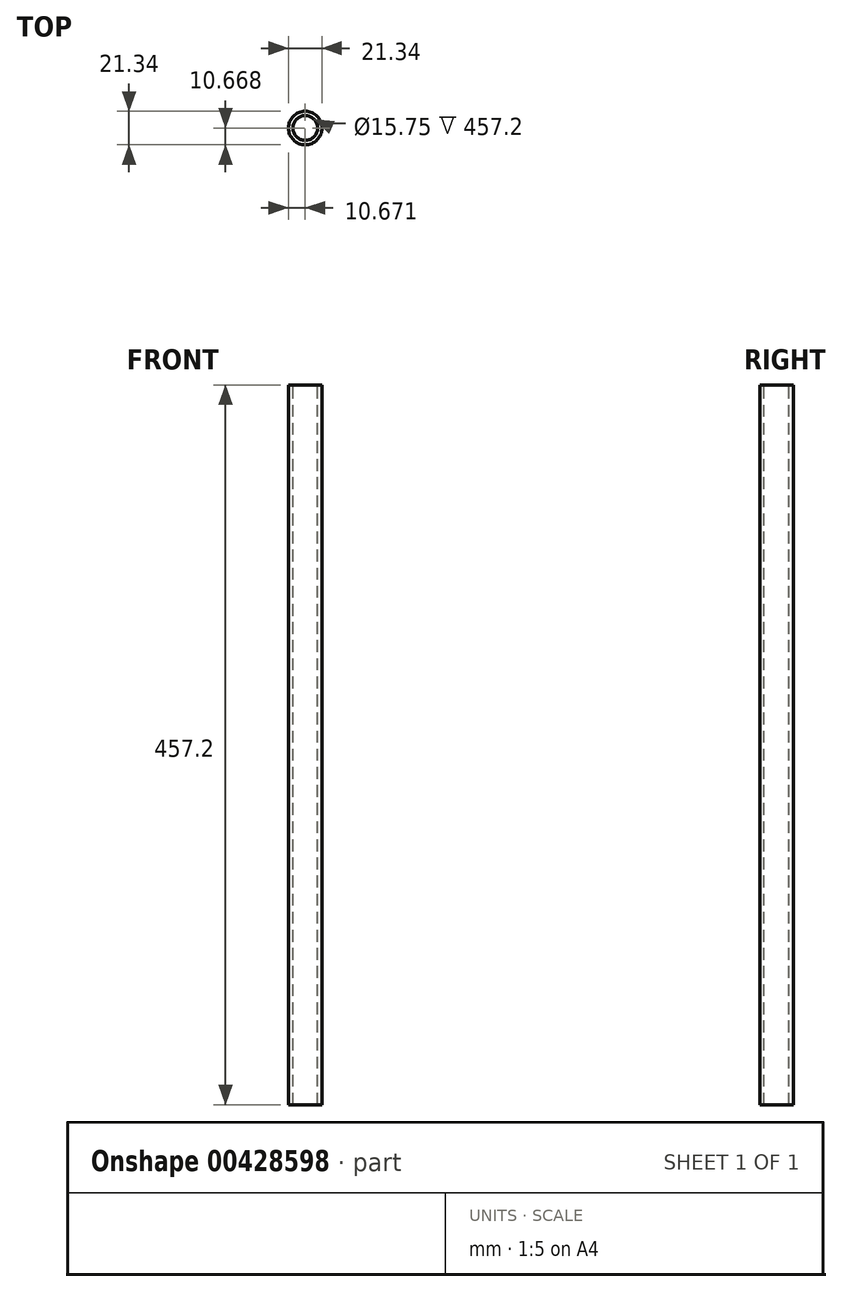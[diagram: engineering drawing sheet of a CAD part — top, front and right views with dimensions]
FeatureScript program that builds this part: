
annotation { "Feature Type Name" : "Feature", "Feature Type Description" : "" }
export const myFeature = defineFeature(function(context is Context, id is Id, definition is map)
    precondition{}
    {
        {
            var Q0;
            Q0=qCreatedBy(makeId("Top.planeOp"),FACE);
            var sketch = newSketch(context, id + "F0", { "sketchPlane" : qUnion([Q0])});
            skCircle(sketch, "E0", {"center": v(72.06, 47.03) * mm, "radius": 10.67 * mm});
            skSolve(sketch);
        }
        {
            var Q0;
            Q0=makeQuery(id+"F0.imprint","IMPRINT",FACE,{"disambiguationData":[TD([[makeQuery(id+"F0.imprint","IMPRINT",EDGE,{"derivedFrom":sQuery(id+"F0.wireOp",EDGE,"E0")}),1.0]])]});
            var sketch = newSketch(context, id + "F1", { "sketchPlane" : qUnion([Q0])});
            skCircle(sketch, "E1", {"center": v(72.06, 47.03) * mm, "radius": 7.87 * mm});
            skSolve(sketch);
        }
        {
            var Q0;
            Q0=makeQuery(id+"F1.imprint","IMPRINT",FACE,{"disambiguationData":[TD([[makeQuery(id+"F1.imprint","IMPRINT",EDGE,{"derivedFrom":sQuery(id+"F1.wireOp",EDGE,"E1")}),-1.0]])]});
            extrude(context, id + "F2", {"entities" : qUnion([Q0]), "oppositeDirection" : true, "depth" : 457.2 * mm});
        }
    });
